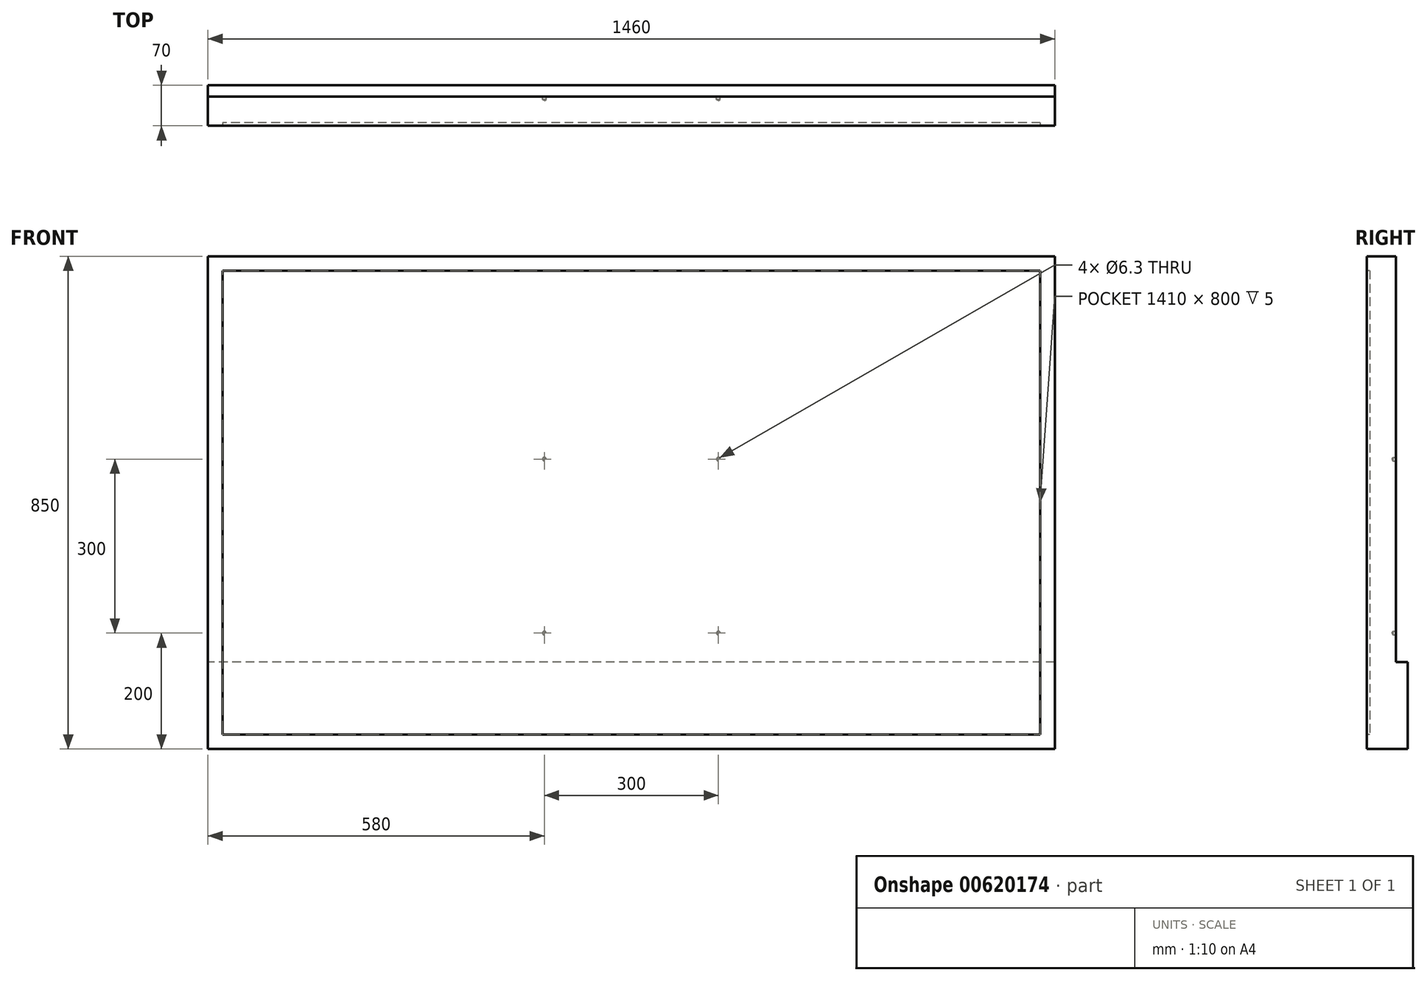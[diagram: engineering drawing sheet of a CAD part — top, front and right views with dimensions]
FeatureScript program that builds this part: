
annotation { "Feature Type Name" : "Feature", "Feature Type Description" : "" }
export const myFeature = defineFeature(function(context is Context, id is Id, definition is map)
    precondition{}
    {
        {
            var Q0;
            Q0=qCreatedBy(makeId("Front.planeOp"),FACE);
            var sketch = newSketch(context, id + "F0", { "sketchPlane" : qUnion([Q0])});
            skLineSegment(sketch, "E0.bottom", {"start": v(730, 425) * mm, "end": v(-730, 425) * mm});
            skLineSegment(sketch, "E0.top", {"start": v(730, -425) * mm, "end": v(-730, -425) * mm});
            skLineSegment(sketch, "E0.left", {"start": v(730, 425) * mm, "end": v(730, -425) * mm});
            skLineSegment(sketch, "E0.right", {"start": v(-730, 425) * mm, "end": v(-730, -425) * mm});
            skPoint(sketch, "E0.middle", {"position": v(0, 0) * mm});
            skSolve(sketch);
        }
        {
            var Q0;
            Q0=makeQuery(id+"F0.imprint","IMPRINT",FACE,{"disambiguationData":[TD([[makeQuery(id+"F0.imprint","IMPRINT",EDGE,{"derivedFrom":sQuery(id+"F0.wireOp",EDGE,"E0.bottom")}),1.0]])]});
            extrude(context, id + "F1", {"entities" : qUnion([Q0]), "depth" : 50 * mm, "offsetDistance" : 25 * mm});
        }
        {
            var Q0;
            Q0=makeQuery(id+"F1.opExtrude","CAP_FACE",FACE,{"disambiguationData":[OSD([sQuery(id+"F0.wireOp",EDGE,"E0.bottom"),sQuery(id+"F0.wireOp",EDGE,"E0.top"),sQuery(id+"F0.wireOp",EDGE,"E0.left"),sQuery(id+"F0.wireOp",EDGE,"E0.right")])],"isStart":false});
            var sketch = newSketch(context, id + "F2", { "sketchPlane" : qUnion([Q0])});
            skLineSegment(sketch, "E1.0", {"start": v(705, 400) * mm, "end": v(-705, 400) * mm});
            skLineSegment(sketch, "E1.1", {"start": v(705, 400) * mm, "end": v(705, -400) * mm});
            skLineSegment(sketch, "E1.2", {"start": v(705, -400) * mm, "end": v(-705, -400) * mm});
            skLineSegment(sketch, "E1.3", {"start": v(-705, 400) * mm, "end": v(-705, -400) * mm});
            skSolve(sketch);
        }
        {
            var Q0;
            Q0=makeQuery(id+"F2.imprint","IMPRINT",FACE,{"disambiguationData":[TD([[makeQuery(id+"F2.imprint","IMPRINT",EDGE,{"derivedFrom":sQuery(id+"F2.wireOp",EDGE,"E1.0")}),1.0]])]});
            extrude(context, id + "F3", {"entities" : qUnion([Q0]), "operationType" : NewBodyOperationType.REMOVE, "oppositeDirection" : true, "depth" : 5 * mm, "offsetDistance" : 25 * mm});
        }
        {
            var Q0;
            Q0=makeQuery(id+"F1.opExtrude","CAP_FACE",FACE,{"disambiguationData":[OSD([sQuery(id+"F0.wireOp",EDGE,"E0.bottom"),sQuery(id+"F0.wireOp",EDGE,"E0.top"),sQuery(id+"F0.wireOp",EDGE,"E0.left"),sQuery(id+"F0.wireOp",EDGE,"E0.right")])],"isStart":true});
            var sketch = newSketch(context, id + "F4", { "sketchPlane" : qUnion([Q0])});
            skLineSegment(sketch, "E2.bottom", {"start": v(150, 75) * mm, "end": v(-150, 75) * mm, "construction": true});
            skLineSegment(sketch, "E2.top", {"start": v(150, -225) * mm, "end": v(-150, -225) * mm, "construction": true});
            skLineSegment(sketch, "E2.left", {"start": v(150, 75) * mm, "end": v(150, -225) * mm, "construction": true});
            skLineSegment(sketch, "E2.right", {"start": v(-150, 75) * mm, "end": v(-150, -225) * mm, "construction": true});
            skPoint(sketch, "E2.middle", {"position": v(0, 0) * mm});
            skLineSegment(sketch, "E3.bottom", {"start": v(-730, -425) * mm, "end": v(730, -425) * mm});
            skLineSegment(sketch, "E3.top", {"start": v(-730, -275) * mm, "end": v(730, -275) * mm});
            skLineSegment(sketch, "E3.left", {"start": v(-730, -425) * mm, "end": v(-730, -275) * mm});
            skLineSegment(sketch, "E3.right", {"start": v(730, -425) * mm, "end": v(730, -275) * mm});
            skLineSegment(sketch, "E4", {"start": v(0, 75) * mm, "end": v(0, -225) * mm, "construction": true});
            skSolve(sketch);
        }
        {
            var Q0;
            Q0=sQuery(id+"F4.wireOp",VERTEX,"E2.right.start");
            var Q1;
            Q1=sQuery(id+"F4.wireOp",VERTEX,"E2.bottom.start");
            var Q2;
            Q2=sQuery(id+"F4.wireOp",VERTEX,"E2.left.end");
            var Q3;
            Q3=sQuery(id+"F4.wireOp",VERTEX,"E2.top.end");
            var Q4;
            Q4=makeQuery(id+"F1.opExtrude","SWEPT_BODY",BODY,{"disambiguationData":[OSD([sQuery(id+"F0.wireOp",EDGE,"E0.bottom"),sQuery(id+"F0.wireOp",EDGE,"E0.top"),sQuery(id+"F0.wireOp",EDGE,"E0.left"),sQuery(id+"F0.wireOp",EDGE,"E0.right")])]});
            hole(context, id + "F5", {"style" : HoleStyle.SIMPLE, "endStyle" : HoleEndStyle.BLIND, "holeDiameter" : 6.3 * mm, "majorDiameter" : 5 * mm, "holeDepth" : 5 * mm, "isTappedThrough" : true, "tappedDepth" : 12 * mm, "tapClearance" : 3, "locations" : qUnion([Q0, Q1, Q2, Q3]), "scope" : qUnion([Q4])});
        }
        {
            var Q0;
            Q0=makeQuery(id+"F4.imprint","IMPRINT",FACE,{"disambiguationData":[TD([[makeQuery(id+"F4.imprint","IMPRINT",EDGE,{"derivedFrom":sQuery(id+"F4.wireOp",EDGE,"E3.bottom")}),1.0]])]});
            extrude(context, id + "F6", {"entities" : qUnion([Q0]), "operationType" : NewBodyOperationType.ADD, "depth" : 20 * mm, "offsetDistance" : 25 * mm});
        }
    });
